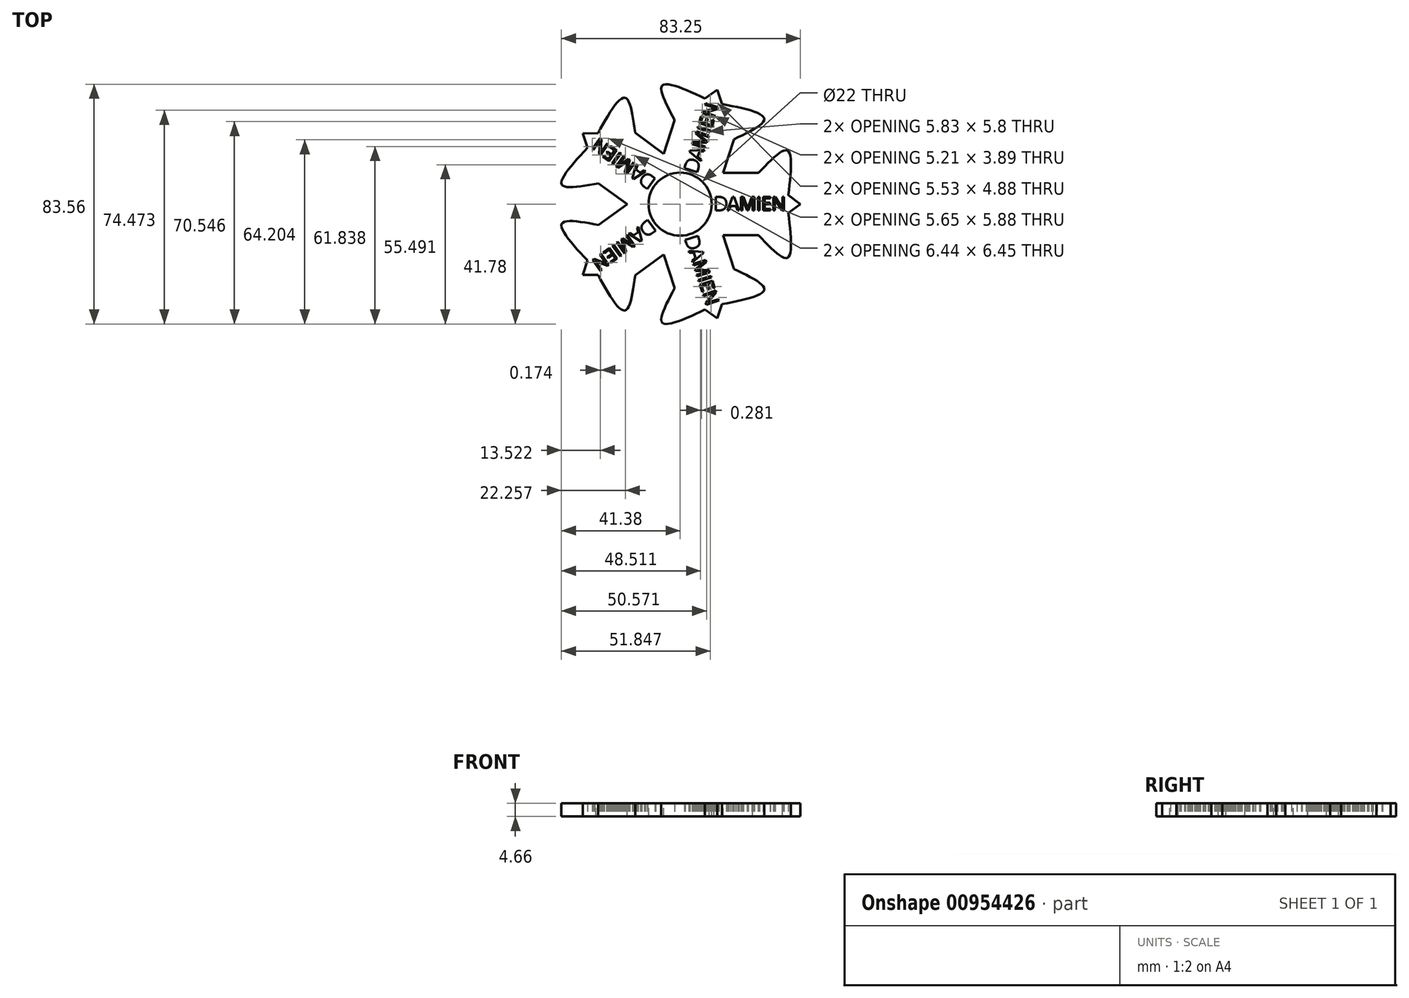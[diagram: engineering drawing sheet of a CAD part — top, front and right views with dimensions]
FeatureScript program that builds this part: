
annotation { "Feature Type Name" : "Feature", "Feature Type Description" : "" }
export const myFeature = defineFeature(function(context is Context, id is Id, definition is map)
    precondition{}
    {
        {
            var Q0;
            Q0=qCreatedBy(makeId("Top.planeOp"),FACE);
            var sketch = newSketch(context, id + "F0", { "sketchPlane" : qUnion([Q0])});
            skCircle(sketch, "E0", {"center": v(0, 0) * mm, "radius": 11 * mm});
            skArc(sketch, "E1", {"start": v(0, 17.5) * mm, "mid": v(-17.5, 0) * mm, "end": v(0, -17.5) * mm});
            skLineSegment(sketch, "E2", {"start": v(0, 0) * mm, "end": v(44, 0) * mm, "construction": true});
            skArc(sketch, "E3", {"start": v(60.76, -5.05) * mm, "mid": v(60.76, -5.04) * mm, "end": v(60.76, -5.04) * mm});
            skLineSegment(sketch, "E4", {"start": v(0, 17.5) * mm, "end": v(44, 17.5) * mm});
            skLineSegment(sketch, "E5", {"start": v(0, -17.5) * mm, "end": v(44, -17.5) * mm});
            skText(sketch, "E6", { "text": "DAMIEN\n", "fontName": "OpenSans-Regular.ttf"});
            skLineSegment(sketch, "E7", {"start": v(60.76, 5.04) * mm, "end": v(67.53, 0) * mm});
            skLineSegment(sketch, "E8.trimOffspring", {"start": v(44, 17.5) * mm, "end": v(44, 17.5) * mm});
            skFitSpline(sketch, "E9", {"points": [v(44, 17.5) * mm, v(60.3, 30.15) * mm, v(60.76, 5.04) * mm], "startDerivative": vector(41.86, 43.85) * mm, "endDerivative": vector(-8.42, -65.5) * mm});
            skFitSpline(sketch, "E10.MirrorCS", {"points": [v(44, -17.5) * mm, v(60.3, -30.15) * mm, v(60.76, -5.04) * mm], "startDerivative": vector(41.86, -43.85) * mm, "endDerivative": vector(-8.42, 65.5) * mm});
            skLineSegment(sketch, "E11", {"start": v(60.76, -5.05) * mm, "end": v(67.53, 0) * mm});
            const initialGuessF0  = {"E6": [0.01896, -0.0035, 1, 0, 0.00754]};
            skSetInitialGuess(sketch, initialGuessF0);
            skSolve(sketch);
        }
        {
            var Q0;
            Q0 = qSketchRegion(id + "F0", true);
            extrude(context, id + "F1", {"entities" : qUnion([Q0]), "endBound" : BoundingType.SYMMETRIC, "depth" : 7.5 * mm, "offsetDistance" : 25 * mm});
        }
        {
            var Q0;
            Q0=makeQuery(id+"F1.opExtrude","SWEPT_BODY",BODY,{"disambiguationData":[OSD([sQuery(id+"F0.wireOp",EDGE,"E0"),sQuery(id+"F0.wireOp",EDGE,"E1"),sQuery(id+"F0.wireOp",EDGE,"E3"),sQuery(id+"F0.wireOp",EDGE,"E4"),sQuery(id+"F0.wireOp",EDGE,"E5")])]});
            var Q1;
            Q1=makeQuery(id+"F1.opExtrude","CAP_EDGE",EDGE,{"disambiguationData":[OSD([sQuery(id+"F0.wireOp",EDGE,"E0")])],"isStart":false});
            circularPattern(context, id + "F2", {"operationType" : NewBodyOperationType.ADD, "entities" : qUnion([Q0]), "axis" : qUnion([Q1]), "angle" : 360 * degree, "instanceCount" : 5, "equalSpace" : true});
        }
        {
            var Q0;
            Q0=makeQuery(id+"F1.opExtrude","SWEPT_BODY",BODY,{"disambiguationData":[OSD([sQuery(id+"F0.wireOp",EDGE,"E0"),sQuery(id+"F0.wireOp",EDGE,"E1"),sQuery(id+"F0.wireOp",EDGE,"E4"),sQuery(id+"F0.wireOp",EDGE,"E5"),sQuery(id+"F0.wireOp",EDGE,"E6.sketch_text.stroke-0"),sQuery(id+"F0.wireOp",EDGE,"E6.sketch_text.stroke-1"),sQuery(id+"F0.wireOp",EDGE,"E6.sketch_text.stroke-2"),sQuery(id+"F0.wireOp",EDGE,"E6.sketch_text.stroke-3"),sQuery(id+"F0.wireOp",EDGE,"E6.sketch_text.stroke-4"),sQuery(id+"F0.wireOp",EDGE,"E6.sketch_text.stroke-5"),sQuery(id+"F0.wireOp",EDGE,"E6.sketch_text.stroke-6"),sQuery(id+"F0.wireOp",EDGE,"E6.sketch_text.stroke-14"),sQuery(id+"F0.wireOp",EDGE,"E6.sketch_text.stroke-15"),sQuery(id+"F0.wireOp",EDGE,"E6.sketch_text.stroke-16"),sQuery(id+"F0.wireOp",EDGE,"E6.sketch_text.stroke-17"),sQuery(id+"F0.wireOp",EDGE,"E6.sketch_text.stroke-18"),sQuery(id+"F0.wireOp",EDGE,"E6.sketch_text.stroke-19"),sQuery(id+"F0.wireOp",EDGE,"E6.sketch_text.stroke-20"),sQuery(id+"F0.wireOp",EDGE,"E6.sketch_text.stroke-21"),sQuery(id+"F0.wireOp",EDGE,"E6.sketch_text.stroke-27"),sQuery(id+"F0.wireOp",EDGE,"E6.sketch_text.stroke-28"),sQuery(id+"F0.wireOp",EDGE,"E6.sketch_text.stroke-29"),sQuery(id+"F0.wireOp",EDGE,"E6.sketch_text.stroke-30"),sQuery(id+"F0.wireOp",EDGE,"E6.sketch_text.stroke-31"),sQuery(id+"F0.wireOp",EDGE,"E6.sketch_text.stroke-32"),sQuery(id+"F0.wireOp",EDGE,"E6.sketch_text.stroke-33"),sQuery(id+"F0.wireOp",EDGE,"E6.sketch_text.stroke-34"),sQuery(id+"F0.wireOp",EDGE,"E6.sketch_text.stroke-35"),sQuery(id+"F0.wireOp",EDGE,"E6.sketch_text.stroke-36"),sQuery(id+"F0.wireOp",EDGE,"E6.sketch_text.stroke-37"),sQuery(id+"F0.wireOp",EDGE,"E6.sketch_text.stroke-38"),sQuery(id+"F0.wireOp",EDGE,"E6.sketch_text.stroke-39"),sQuery(id+"F0.wireOp",EDGE,"E6.sketch_text.stroke-40"),sQuery(id+"F0.wireOp",EDGE,"E6.sketch_text.stroke-41"),sQuery(id+"F0.wireOp",EDGE,"E6.sketch_text.stroke-42"),sQuery(id+"F0.wireOp",EDGE,"E6.sketch_text.stroke-43"),sQuery(id+"F0.wireOp",EDGE,"E6.sketch_text.stroke-44"),sQuery(id+"F0.wireOp",EDGE,"E6.sketch_text.stroke-45"),sQuery(id+"F0.wireOp",EDGE,"E6.sketch_text.stroke-46"),sQuery(id+"F0.wireOp",EDGE,"E6.sketch_text.stroke-47"),sQuery(id+"F0.wireOp",EDGE,"E6.sketch_text.stroke-48"),sQuery(id+"F0.wireOp",EDGE,"E6.sketch_text.stroke-49"),sQuery(id+"F0.wireOp",EDGE,"E6.sketch_text.stroke-50"),sQuery(id+"F0.wireOp",EDGE,"E6.sketch_text.stroke-51"),sQuery(id+"F0.wireOp",EDGE,"E6.sketch_text.stroke-52"),sQuery(id+"F0.wireOp",EDGE,"E6.sketch_text.stroke-53"),sQuery(id+"F0.wireOp",EDGE,"E6.sketch_text.stroke-54"),sQuery(id+"F0.wireOp",EDGE,"E6.sketch_text.stroke-55"),sQuery(id+"F0.wireOp",EDGE,"E6.sketch_text.stroke-56"),sQuery(id+"F0.wireOp",EDGE,"E6.sketch_text.stroke-57"),sQuery(id+"F0.wireOp",EDGE,"E6.sketch_text.stroke-58"),sQuery(id+"F0.wireOp",EDGE,"E6.sketch_text.stroke-59"),sQuery(id+"F0.wireOp",EDGE,"E6.sketch_text.stroke-60"),sQuery(id+"F0.wireOp",EDGE,"E6.sketch_text.stroke-61"),sQuery(id+"F0.wireOp",EDGE,"E6.sketch_text.stroke-62"),sQuery(id+"F0.wireOp",EDGE,"E6.sketch_text.stroke-63"),sQuery(id+"F0.wireOp",EDGE,"E6.sketch_text.stroke-64"),sQuery(id+"F0.wireOp",EDGE,"E6.sketch_text.stroke-65"),sQuery(id+"F0.wireOp",EDGE,"E6.sketch_text.stroke-66"),sQuery(id+"F0.wireOp",EDGE,"E6.sketch_text.stroke-67"),sQuery(id+"F0.wireOp",EDGE,"E6.sketch_text.stroke-68"),sQuery(id+"F0.wireOp",EDGE,"E6.sketch_text.stroke-69"),sQuery(id+"F0.wireOp",EDGE,"E6.sketch_text.stroke-70"),sQuery(id+"F0.wireOp",EDGE,"E6.sketch_text.stroke-71"),sQuery(id+"F0.wireOp",EDGE,"E6.sketch_text.stroke-72"),sQuery(id+"F0.wireOp",EDGE,"E6.sketch_text.stroke-73"),sQuery(id+"F0.wireOp",EDGE,"E6.sketch_text.stroke-74"),sQuery(id+"F0.wireOp",EDGE,"E6.sketch_text.stroke-75"),sQuery(id+"F0.wireOp",EDGE,"E7"),sQuery(id+"F0.wireOp",EDGE,"E9"),sQuery(id+"F0.wireOp",EDGE,"E10.MirrorCS"),sQuery(id+"F0.wireOp",EDGE,"E11")])]});
            var Q1;
            Q1=qCreatedBy(makeId("Origin.pointOp"),VERTEX);
            transform(context, id + "F3", {"entities" : qUnion([Q0]), "transformType" : TransformType.SCALE_UNIFORMLY, "scale" : .62, "scalePoint" : qUnion([Q1]), "makeCopy" : false});
        }
        {
            var Q0;
            {var subQ0=makeQuery(id+"F1.opExtrude","CAP_FACE",FACE,{"disambiguationData":[OSD([sQuery(id+"F0.wireOp",EDGE,"E0"),sQuery(id+"F0.wireOp",EDGE,"E1"),sQuery(id+"F0.wireOp",EDGE,"E4"),sQuery(id+"F0.wireOp",EDGE,"E5"),sQuery(id+"F0.wireOp",EDGE,"E6.sketch_text.stroke-0"),sQuery(id+"F0.wireOp",EDGE,"E6.sketch_text.stroke-1"),sQuery(id+"F0.wireOp",EDGE,"E6.sketch_text.stroke-2"),sQuery(id+"F0.wireOp",EDGE,"E6.sketch_text.stroke-3"),sQuery(id+"F0.wireOp",EDGE,"E6.sketch_text.stroke-4"),sQuery(id+"F0.wireOp",EDGE,"E6.sketch_text.stroke-5"),sQuery(id+"F0.wireOp",EDGE,"E6.sketch_text.stroke-6"),sQuery(id+"F0.wireOp",EDGE,"E6.sketch_text.stroke-14"),sQuery(id+"F0.wireOp",EDGE,"E6.sketch_text.stroke-15"),sQuery(id+"F0.wireOp",EDGE,"E6.sketch_text.stroke-16"),sQuery(id+"F0.wireOp",EDGE,"E6.sketch_text.stroke-17"),sQuery(id+"F0.wireOp",EDGE,"E6.sketch_text.stroke-18"),sQuery(id+"F0.wireOp",EDGE,"E6.sketch_text.stroke-19"),sQuery(id+"F0.wireOp",EDGE,"E6.sketch_text.stroke-20"),sQuery(id+"F0.wireOp",EDGE,"E6.sketch_text.stroke-21"),sQuery(id+"F0.wireOp",EDGE,"E6.sketch_text.stroke-27"),sQuery(id+"F0.wireOp",EDGE,"E6.sketch_text.stroke-28"),sQuery(id+"F0.wireOp",EDGE,"E6.sketch_text.stroke-29"),sQuery(id+"F0.wireOp",EDGE,"E6.sketch_text.stroke-30"),sQuery(id+"F0.wireOp",EDGE,"E6.sketch_text.stroke-31"),sQuery(id+"F0.wireOp",EDGE,"E6.sketch_text.stroke-32"),sQuery(id+"F0.wireOp",EDGE,"E6.sketch_text.stroke-33"),sQuery(id+"F0.wireOp",EDGE,"E6.sketch_text.stroke-34"),sQuery(id+"F0.wireOp",EDGE,"E6.sketch_text.stroke-35"),sQuery(id+"F0.wireOp",EDGE,"E6.sketch_text.stroke-36"),sQuery(id+"F0.wireOp",EDGE,"E6.sketch_text.stroke-37"),sQuery(id+"F0.wireOp",EDGE,"E6.sketch_text.stroke-38"),sQuery(id+"F0.wireOp",EDGE,"E6.sketch_text.stroke-39"),sQuery(id+"F0.wireOp",EDGE,"E6.sketch_text.stroke-40"),sQuery(id+"F0.wireOp",EDGE,"E6.sketch_text.stroke-41"),sQuery(id+"F0.wireOp",EDGE,"E6.sketch_text.stroke-42"),sQuery(id+"F0.wireOp",EDGE,"E6.sketch_text.stroke-43"),sQuery(id+"F0.wireOp",EDGE,"E6.sketch_text.stroke-44"),sQuery(id+"F0.wireOp",EDGE,"E6.sketch_text.stroke-45"),sQuery(id+"F0.wireOp",EDGE,"E6.sketch_text.stroke-46"),sQuery(id+"F0.wireOp",EDGE,"E6.sketch_text.stroke-47"),sQuery(id+"F0.wireOp",EDGE,"E6.sketch_text.stroke-48"),sQuery(id+"F0.wireOp",EDGE,"E6.sketch_text.stroke-49"),sQuery(id+"F0.wireOp",EDGE,"E6.sketch_text.stroke-50"),sQuery(id+"F0.wireOp",EDGE,"E6.sketch_text.stroke-51"),sQuery(id+"F0.wireOp",EDGE,"E6.sketch_text.stroke-52"),sQuery(id+"F0.wireOp",EDGE,"E6.sketch_text.stroke-53"),sQuery(id+"F0.wireOp",EDGE,"E6.sketch_text.stroke-54"),sQuery(id+"F0.wireOp",EDGE,"E6.sketch_text.stroke-55"),sQuery(id+"F0.wireOp",EDGE,"E6.sketch_text.stroke-56"),sQuery(id+"F0.wireOp",EDGE,"E6.sketch_text.stroke-57"),sQuery(id+"F0.wireOp",EDGE,"E6.sketch_text.stroke-58"),sQuery(id+"F0.wireOp",EDGE,"E6.sketch_text.stroke-59"),sQuery(id+"F0.wireOp",EDGE,"E6.sketch_text.stroke-60"),sQuery(id+"F0.wireOp",EDGE,"E6.sketch_text.stroke-61"),sQuery(id+"F0.wireOp",EDGE,"E6.sketch_text.stroke-62"),sQuery(id+"F0.wireOp",EDGE,"E6.sketch_text.stroke-63"),sQuery(id+"F0.wireOp",EDGE,"E6.sketch_text.stroke-64"),sQuery(id+"F0.wireOp",EDGE,"E6.sketch_text.stroke-65"),sQuery(id+"F0.wireOp",EDGE,"E6.sketch_text.stroke-66"),sQuery(id+"F0.wireOp",EDGE,"E6.sketch_text.stroke-67"),sQuery(id+"F0.wireOp",EDGE,"E6.sketch_text.stroke-68"),sQuery(id+"F0.wireOp",EDGE,"E6.sketch_text.stroke-69"),sQuery(id+"F0.wireOp",EDGE,"E6.sketch_text.stroke-70"),sQuery(id+"F0.wireOp",EDGE,"E6.sketch_text.stroke-71"),sQuery(id+"F0.wireOp",EDGE,"E6.sketch_text.stroke-72"),sQuery(id+"F0.wireOp",EDGE,"E6.sketch_text.stroke-73"),sQuery(id+"F0.wireOp",EDGE,"E6.sketch_text.stroke-74"),sQuery(id+"F0.wireOp",EDGE,"E6.sketch_text.stroke-75"),sQuery(id+"F0.wireOp",EDGE,"E7"),sQuery(id+"F0.wireOp",EDGE,"E9"),sQuery(id+"F0.wireOp",EDGE,"E10.MirrorCS"),sQuery(id+"F0.wireOp",EDGE,"E11")])],"isStart":false});Q0=makeQuery(id+"F2.boolean.opBoolean","MERGE",FACE,{"derivedFrom":[subQ0,makeQuery(id+"F2.opPattern","COPY",FACE,{"derivedFrom":subQ0,"instanceName":"1"}),makeQuery(id+"F2.opPattern","COPY",FACE,{"derivedFrom":subQ0,"instanceName":"2"}),makeQuery(id+"F2.opPattern","COPY",FACE,{"derivedFrom":subQ0,"instanceName":"3"}),makeQuery(id+"F2.opPattern","COPY",FACE,{"derivedFrom":subQ0,"instanceName":"4"})]});}
            var sketch = newSketch(context, id + "F4", { "sketchPlane" : qUnion([Q0])});
            skPoint(sketch, "E12.0", {"position": v(0, 0) * mm});
            skCircle(sketch, "E13", {"center": v(0, 0) * mm, "radius": 11 * mm});
            skSolve(sketch);
        }
        {
            var Q0;
            Q0 = qSketchRegion(id + "F4", true);
            extrude(context, id + "F5", {"entities" : qUnion([Q0]), "operationType" : NewBodyOperationType.REMOVE, "oppositeDirection" : true, "depth" : 25 * mm, "offsetDistance" : 25 * mm});
        }
    });
